# Revit family: Pipefitting_IBP_Conex_MaxiPro_Tee_MP5130
name_source: partatom
category: Pipe Fittings
units: mm (PartAtom-declared; Revit-internal decimal feet)

## family parameters
Always vertical = No
Cut with Voids When Loaded = No
OmniClass Number = 23.65.00.00
OmniClass Title = Supply and Distribution of Liquids and Gases
Part Type = Tee
Round Connector Dimension = Use Diameter
Shared = No
Work Plane-Based = No

## types (8) — shared parameters
Application = Air conditioning & refrigeration
Assembly Code = D20
AssetType = Fixed
BIMObjectName = PipeFitting_IBP_Conex_MaxiPro_EqualTee_MP5130
ClassificationName = Uniclass2015
ClassificationValue = Pr_65_52_63_18
Description = Equal Tee
ExpectedServiceLifeYears = 25
FittingType = Equal Tee
FluidTemperatureMax = 121 °C
FluidTemperatureMin = -40 °C
IfcExportAs = IfcPipeFitting
IfcExportType = IfcPipeFittingType
Keynote = S
Manufacturer = Conex Banninger
ManufacturerName = IBP
Material = Copper, C12200
MaterialType = Refrigerant Grade Copper, C12200
MaxHydrostaticPressure = 48 bar
NBSDescription = Copper pipeline fittings
NBSObjectName = IBP - Copper pipeline fittings
NBSReference = 90-10-65/315
ORingTemperatureRange = -40°C to 140°C
PipeConnectorType = Press x Press
PressJawCompatability = MaxiPro Jaws supplied by Rothenberger
ProductionYear = 2016
SealType = HNBR
Shape = Cylindrical
SurfaceFinish = Natural
URL = http://www.conexbanninger.com
WarrantyDescription = Product Guarantee
WarrantyDurationMonths = 60
Weight = 0.00 kg
_BimstoreBibleVersion = 14
_CurrentRevision = 1
_DistributedBy = www.bimmepaus.com.au/
zero-valued in all types: NominalDepth, NominalHeight, NominalLength, _BimSpecGuid

## per-type parameters (varying)
| type | A_Length | AnnotationBranchLength_Formula | B | B_TubeStop_Formula | BeadDepth_Branch_Formula | BeadDepth_Formula | Bead_Depth | Bead_Dia | C_BranchLength | D1_Body_OD | D_BranchTubeStop | ID_ConnectionSize | Model | ModelNumber | ProductCode |
| MP5130 0020202 1/4" Equal Tee | 54 mm | 27 mm  [stored 0.0885827 ft] | 9 mm  [stored 0.0295276 ft] | 18 mm  [stored 0.0590551 ft] | 20 mm | 39 mm  [stored 0.127953 ft] | 8 mm  [stored 0.0262467 ft] | 2 mm  [stored 0.00656168 ft] | 27 mm  [stored 0.0885827 ft] | 8 mm  [stored 0.0262467 ft] | 9 mm  [stored 0.0295276 ft] | 6 mm  [stored 0.019685 ft] | MP5130 0020202 | MP5130 0020202 | MP5130 0020202 |
| MP5130 0030303 3/8" Equal Tee | 63 mm | 32 mm | 9 mm  [stored 0.0295276 ft] | 18 mm  [stored 0.0590551 ft] | 20 mm | 49 mm | 7 mm  [stored 0.0229659 ft] | 3 mm  [stored 0.00984252 ft] | 27 mm  [stored 0.0885827 ft] | 12 mm  [stored 0.0393701 ft] | 13 mm | 10 mm  [stored 0.0328084 ft] | MP5130 0030303 | MP5130 0030303 | MP5130 0030303 |
| MP5130 0040404 1/2" Equal Tee | 66 mm | 33 mm | 14 mm  [stored 0.0459318 ft] | 27 mm  [stored 0.0885827 ft] | 21 mm | 52 mm | 7 mm  [stored 0.0229659 ft] | 3 mm  [stored 0.00984252 ft] | 28 mm | 15 mm  [stored 0.0492126 ft] | 11 mm | 13 mm | MP5130 0040404 | MP5130 0040404 | MP5130 0040404 |
| MP5130 0050505 5/8" Equal Tee | 76 mm | 38 mm | 17 mm | 34 mm | 24 mm | 60 mm | 8 mm  [stored 0.0262467 ft] | 3 mm  [stored 0.00984252 ft] | 32 mm | 19 mm | 11 mm | 16 mm | MP5130 0050505 | MP5130 0050505 | MP5130 0050505 |
| MP5130 0060606 3/4" Equal Tee | 84 mm | 42 mm | 20 mm | 40 mm | 26 mm | 64 mm | 10 mm  [stored 0.0328084 ft] | 4 mm  [stored 0.0131234 ft] | 36 mm | 22 mm  [stored 0.0721785 ft] | 14 mm  [stored 0.0459318 ft] | 19 mm | MP5130 0060606 | MP5130 0060606 | MP5130 0060606 |
| MP5130 0070707 7/8" Equal Tee | 89 mm | 45 mm | 21 mm | 41 mm  [stored 0.134514 ft] | 29 mm | 69 mm | 10 mm  [stored 0.0328084 ft] | 4 mm  [stored 0.0131234 ft] | 39 mm  [stored 0.127953 ft] | 26 mm | 15 mm  [stored 0.0492126 ft] | 22 mm  [stored 0.0721785 ft] | MP5130 0070707 | MP5130 0070707 | MP5130 0070707 |
| MP5130 0080808 1" Equal Tee | 92 mm | 46 mm | 23 mm | 45 mm | 31 mm | 74 mm | 9 mm  [stored 0.0295276 ft] | 4 mm  [stored 0.0131234 ft] | 40 mm | 29 mm | 17 mm | 26 mm | MP5130 0080808 | MP5130 0080808 | MP5130 0080808 |
| MP5130 0090909 1 1/8" Equal Tee | 95 mm | 48 mm | 22 mm  [stored 0.0721785 ft] | 44 mm | 34 mm | 77 mm | 9 mm  [stored 0.0295276 ft] | 4 mm  [stored 0.0131234 ft] | 44 mm | 32 mm | 18 mm  [stored 0.0590551 ft] | 29 mm | MP5130 0090909 | MP5130 0090909 | MP5130 0090909 |

note: [stored X ft] marks values corroborated as IEEE doubles in the binary element streams (Revit-internal decimal feet)

## geometry (parser evidence)
native form markers: Sweep x7
no freeform markers — native parametric forms only
